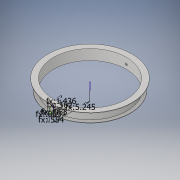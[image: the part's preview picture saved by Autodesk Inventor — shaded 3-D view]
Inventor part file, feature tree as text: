
AUTODESK INVENTOR PART (.ipt)
format: ipt  version: 2017 (Build 210142000, 142)  size: 159,744 bytes
history: native  units: in
note: dims shown in document units (in); Inventor stores cm internally (conversion verified against a paired STEP export)
features: sketch x3, extrude x3, revolve x1, plane x1
ambient origin geometry x8: Origin, YZ Plane, XZ Plane, XY Plane, X Axis, Y Axis, Z Axis, Center Point
bodies: Solid1 (feature_tree)
feature tree (8):
  revolve  "Revolution1"  [1 undecoded]
  plane  "Work Plane1"
  sketch  "Sketch2"  dims[d3=1.4364in d4=0.0625in]
  extrude  "Extrusion2"  Depth=0.0625in
  extrude  "Extrusion3"  TaperAngle=90.0deg  [1 undecoded]
  extrude  "Extrusion4"  Depth=0.0625in
  sketch  "Sketch1"  dims[d1=0.5536in d2=0.0625in]
  sketch  "Sketch3"  dims[d5=0.0625in d6=90.0deg d7=0.562in d8=0.375in d11=0.3125in d12=1.0in d13=0.0in d14=0.0156in d15=0.0in d16=0.25in d17=0.0625in d18=0.0in]
note: 2 required parameter values undecoded (feature->parameter linkage not recoverable at this tier; creation-order binding heuristic only, values carry confidence <= 0.55)